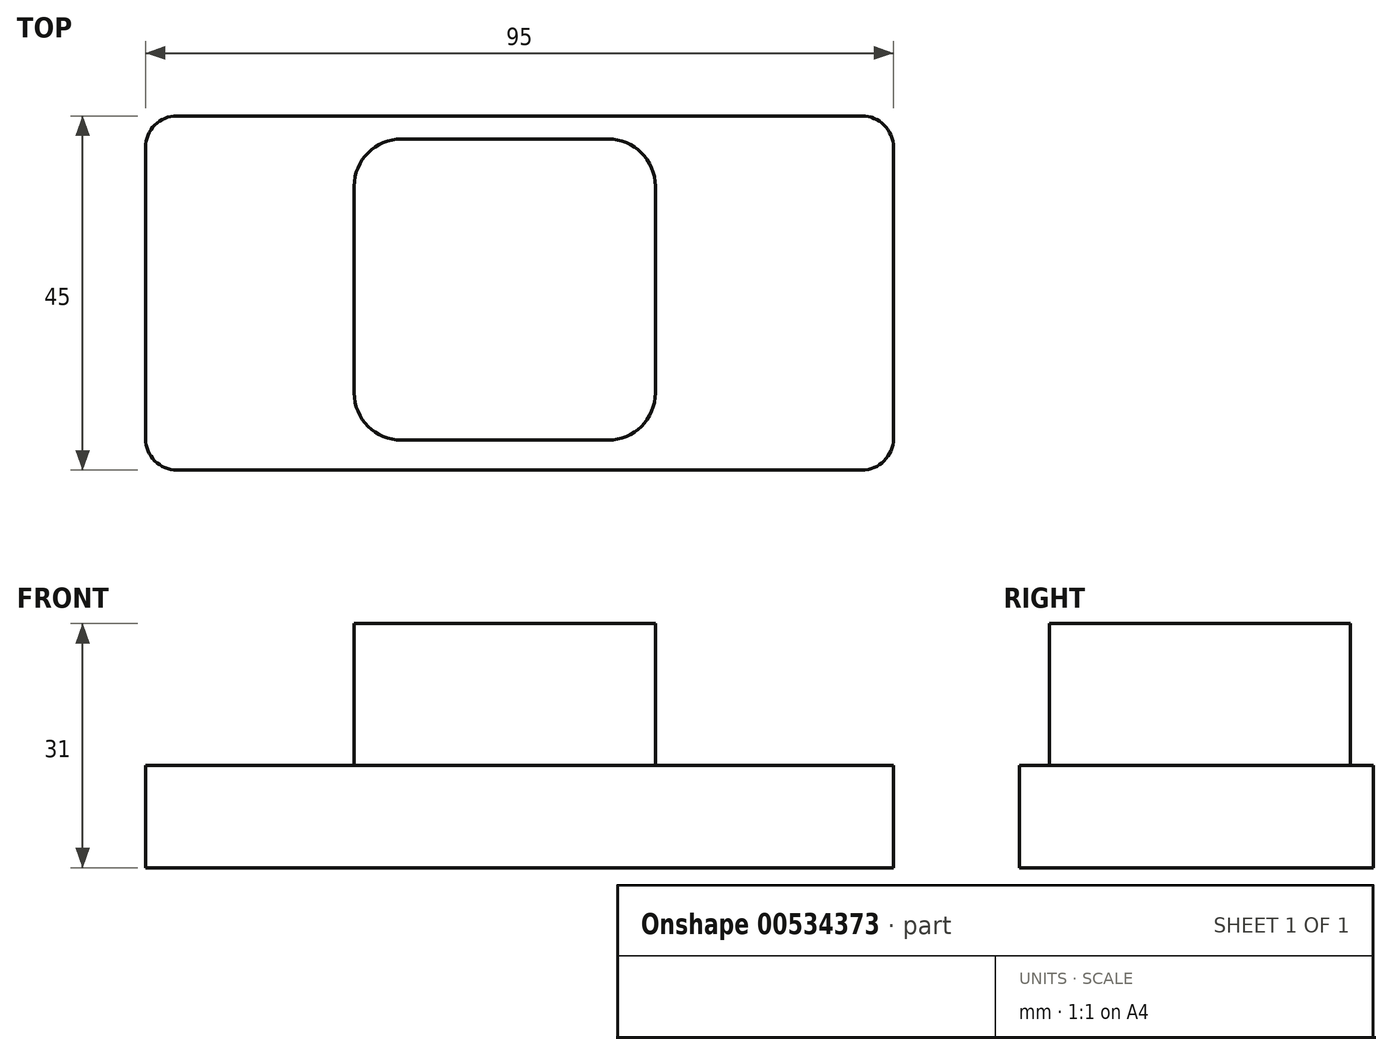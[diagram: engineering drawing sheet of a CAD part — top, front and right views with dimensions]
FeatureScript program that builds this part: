
annotation { "Feature Type Name" : "Feature", "Feature Type Description" : "" }
export const myFeature = defineFeature(function(context is Context, id is Id, definition is map)
    precondition{}
    {
        {
            var Q0;
            Q0=qCreatedBy(makeId("Top.planeOp"),FACE);
            var sketch = newSketch(context, id + "F0", { "sketchPlane" : qUnion([Q0])});
            skLineSegment(sketch, "E0.bottom", {"start": v(47.5, -22.5) * mm, "end": v(-47.5, -22.5) * mm});
            skLineSegment(sketch, "E0.top", {"start": v(47.5, 22.5) * mm, "end": v(-47.5, 22.5) * mm});
            skLineSegment(sketch, "E0.left", {"start": v(47.5, -22.5) * mm, "end": v(47.5, 22.5) * mm});
            skLineSegment(sketch, "E0.right", {"start": v(-47.5, -22.5) * mm, "end": v(-47.5, 22.5) * mm});
            skPoint(sketch, "E0.middle", {"position": v(0, 0) * mm});
            skLineSegment(sketch, "E1.bottom", {"start": v(-21, 19.56) * mm, "end": v(17.25, 19.56) * mm});
            skLineSegment(sketch, "E1.top", {"start": v(-21, -18.69) * mm, "end": v(17.25, -18.69) * mm});
            skLineSegment(sketch, "E1.left", {"start": v(-21, 19.56) * mm, "end": v(-21, -18.69) * mm});
            skLineSegment(sketch, "E1.right", {"start": v(17.25, 19.56) * mm, "end": v(17.25, -18.69) * mm});
            skSolve(sketch);
        }
        {
            var Q0;
            Q0=makeQuery(id+"F0.imprint","IMPRINT",FACE,{"disambiguationData":[TD([[makeQuery(id+"F0.imprint","IMPRINT",EDGE,{"derivedFrom":sQuery(id+"F0.wireOp",EDGE,"E1.bottom")}),-1.0]])]});
            extrude(context, id + "F1", {"entities" : qUnion([Q0]), "depth" : 31 * mm, "offsetDistance" : 25 * mm});
        }
        {
            var Q0;
            Q0=makeQuery(id+"F0.imprint","IMPRINT",FACE,{"disambiguationData":[TD([[makeQuery(id+"F0.imprint","IMPRINT",EDGE,{"derivedFrom":sQuery(id+"F0.wireOp",EDGE,"E0.bottom")}),-1.0]])]});
            extrude(context, id + "F2", {"entities" : qUnion([Q0]), "operationType" : NewBodyOperationType.ADD, "depth" : 13 * mm, "offsetDistance" : 25 * mm});
        }
        {
            var Q0;
            Q0=makeQuery(id+"F1.opExtrude","SWEPT_EDGE",EDGE,{"disambiguationData":[OSD([sQuery(id+"F0.wireOp",EDGE,"E1.bottom"),sQuery(id+"F0.wireOp",EDGE,"E1.left")])]});
            var Q1;
            Q1=makeQuery(id+"F1.opExtrude","SWEPT_EDGE",EDGE,{"disambiguationData":[OSD([sQuery(id+"F0.wireOp",EDGE,"E1.top"),sQuery(id+"F0.wireOp",EDGE,"E1.left")])]});
            var Q2;
            Q2=makeQuery(id+"F1.opExtrude","SWEPT_EDGE",EDGE,{"disambiguationData":[OSD([sQuery(id+"F0.wireOp",EDGE,"E1.top"),sQuery(id+"F0.wireOp",EDGE,"E1.right")])]});
            var Q3;
            Q3=makeQuery(id+"F1.opExtrude","SWEPT_EDGE",EDGE,{"disambiguationData":[OSD([sQuery(id+"F0.wireOp",EDGE,"E1.bottom"),sQuery(id+"F0.wireOp",EDGE,"E1.right")])]});
            fillet(context, id + "F3", {"entities" : qUnion([Q0, Q1, Q2, Q3]), "radius" : 6 * mm, "tangentPropagation" : true, "allowEdgeOverflow" : false});
        }
        {
            var Q0;
            Q0=makeQuery(id+"F2.opExtrude","SWEPT_EDGE",EDGE,{"disambiguationData":[OSD([sQuery(id+"F0.wireOp",EDGE,"E0.bottom"),sQuery(id+"F0.wireOp",EDGE,"E0.left")])]});
            var Q1;
            Q1=makeQuery(id+"F2.opExtrude","SWEPT_EDGE",EDGE,{"disambiguationData":[OSD([sQuery(id+"F0.wireOp",EDGE,"E0.top"),sQuery(id+"F0.wireOp",EDGE,"E0.left")])]});
            var Q2;
            Q2=makeQuery(id+"F2.opExtrude","SWEPT_EDGE",EDGE,{"disambiguationData":[OSD([sQuery(id+"F0.wireOp",EDGE,"E0.bottom"),sQuery(id+"F0.wireOp",EDGE,"E0.right")])]});
            var Q3;
            Q3=makeQuery(id+"F2.opExtrude","SWEPT_EDGE",EDGE,{"disambiguationData":[OSD([sQuery(id+"F0.wireOp",EDGE,"E0.top"),sQuery(id+"F0.wireOp",EDGE,"E0.right")])]});
            fillet(context, id + "F4", {"entities" : qUnion([Q0, Q1, Q2, Q3]), "radius" : 4 * mm, "tangentPropagation" : true, "allowEdgeOverflow" : false});
        }
    });
